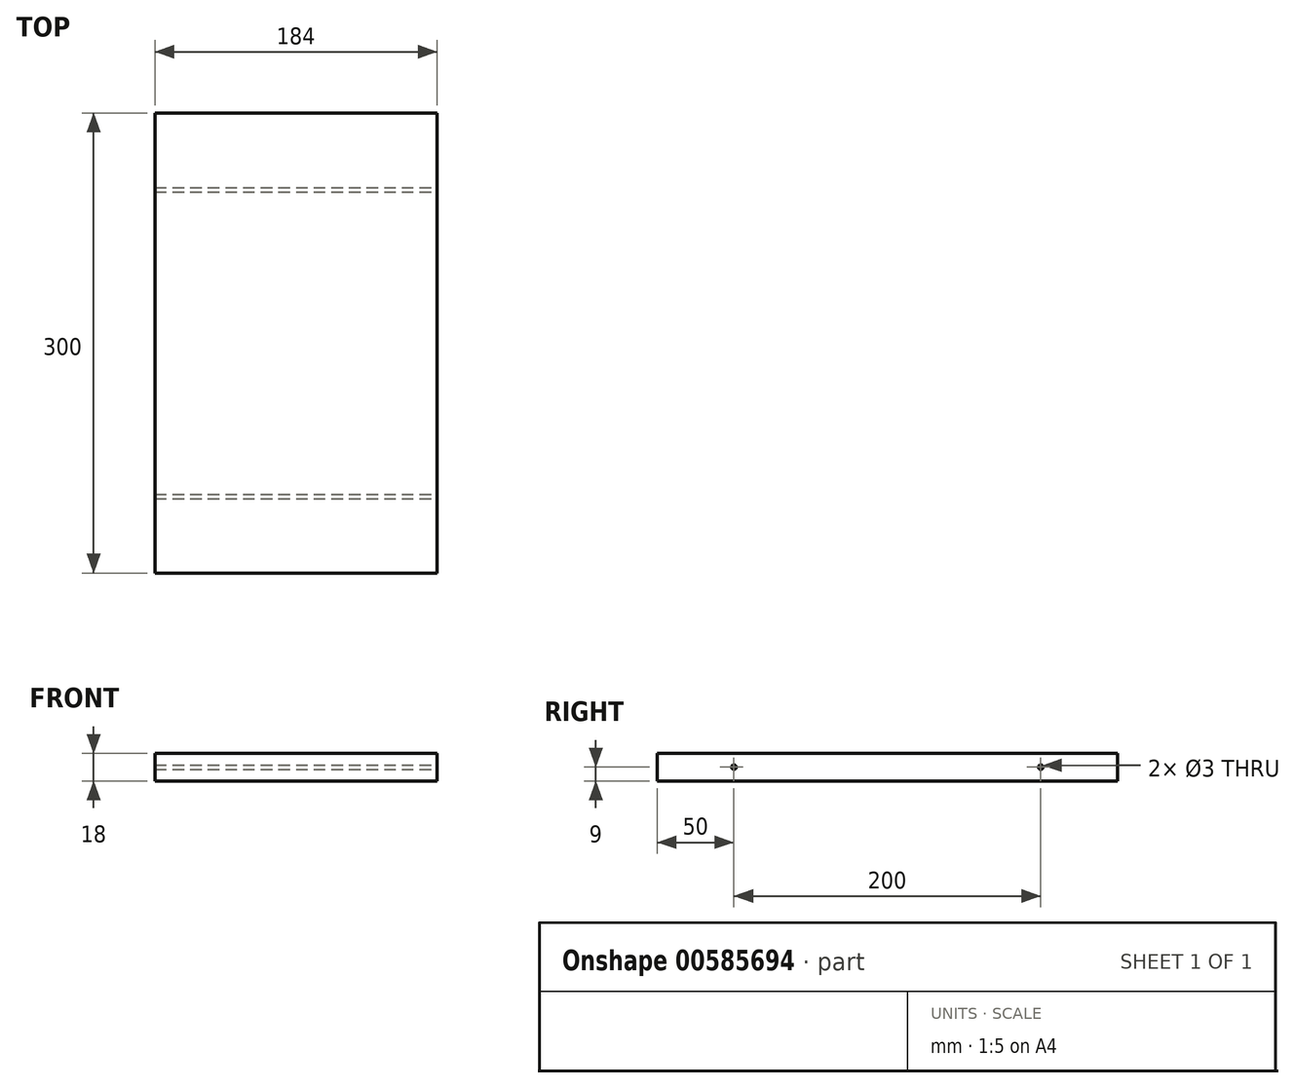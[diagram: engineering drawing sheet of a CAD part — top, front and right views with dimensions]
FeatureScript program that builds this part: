
annotation { "Feature Type Name" : "Feature", "Feature Type Description" : "" }
export const myFeature = defineFeature(function(context is Context, id is Id, definition is map)
    precondition{}
    {
        {
            var Q0;
            Q0=qCreatedBy(makeId("Top.planeOp"),FACE);
            var sketch = newSketch(context, id + "F0", { "sketchPlane" : qUnion([Q0])});
            skLineSegment(sketch, "E0.bottom", {"start": v(0, 0) * mm, "end": v(-184, 0) * mm});
            skLineSegment(sketch, "E0.top", {"start": v(0, -300) * mm, "end": v(-184, -300) * mm});
            skLineSegment(sketch, "E0.left", {"start": v(0, 0) * mm, "end": v(0, -300) * mm});
            skLineSegment(sketch, "E0.right", {"start": v(-184, 0) * mm, "end": v(-184, -300) * mm});
            skSolve(sketch);
        }
        {
            var Q0;
            Q0=makeQuery(id+"F0.imprint","IMPRINT",FACE,{"disambiguationData":[TD([[makeQuery(id+"F0.imprint","IMPRINT",EDGE,{"derivedFrom":sQuery(id+"F0.wireOp",EDGE,"E0.bottom")}),1.0]])]});
            extrude(context, id + "F1", {"entities" : qUnion([Q0]), "depth" : 18 * mm, "offsetDistance" : 25 * mm});
        }
        {
            var Q0;
            Q0=makeQuery(id+"F1.opExtrude","SWEPT_FACE",FACE,{"disambiguationData":[OSD([sQuery(id+"F0.wireOp",EDGE,"E0.left")])]});
            var sketch = newSketch(context, id + "F2", { "sketchPlane" : qUnion([Q0])});
            skCircle(sketch, "E1", {"center": v(-250, 9) * mm, "radius": 1.5 * mm});
            skCircle(sketch, "E2", {"center": v(-50, 9) * mm, "radius": 1.5 * mm});
            skSolve(sketch);
        }
        {
            var Q0;
            Q0 = qSketchRegion(id + "F2", true);
            extrude(context, id + "F3", {"entities" : qUnion([Q0]), "operationType" : NewBodyOperationType.REMOVE, "endBound" : BoundingType.THROUGH_ALL, "oppositeDirection" : true, "depth" : 25 * mm, "offsetDistance" : 25 * mm});
        }
    });
